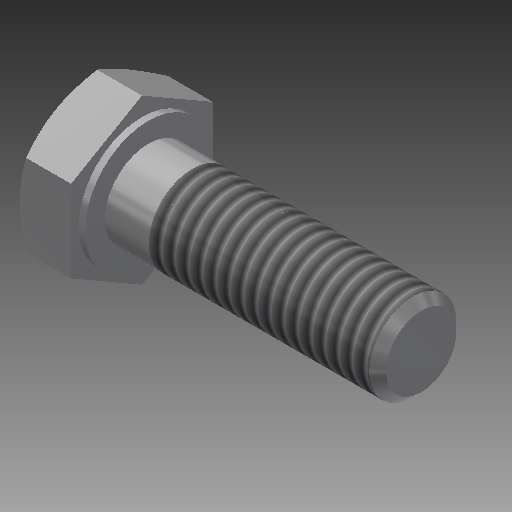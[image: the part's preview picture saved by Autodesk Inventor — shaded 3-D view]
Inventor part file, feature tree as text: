
AUTODESK INVENTOR PART (.ipt)
format: ipt  version: 2017 SP1 (Build 210196100, 196)  size: 233,472 bytes
history: native  units: mm (DEFAULTED — no unit token found)
features: sketch x3, extrude x1, chamfer x1
ambient origin geometry x8: Origin, YZ Plane, XZ Plane, XY Plane, X Axis, Y Axis, Z Axis, Center Point
bodies: Solid1 (feature_tree), Body (feature_tree)
feature tree (5):
  extrude  "Head"  Depth=21.0mm
  chamfer  "Chamfer1"  Distance=4.7mm
  sketch  "Sketch1"  dims[d0=25.0mm d1=21.0mm]
  sketch  "Sketch2"  dims[d2=8.0mm]
  sketch  "Sketch4"  dims[d12=90.0deg d3=4.7mm d4=0.0mm d5=30.0deg d21=90.0deg d6=0.766813mm d7=0.766912mm d8=0.0mm d9=0.6001mm d10=11.63mm d11=13.0mm d13=0.766912mm d14=8.0mm d15=21.0mm d16=0.0mm d19=13.0mm d20=-25.0mm d55=45.0deg]
